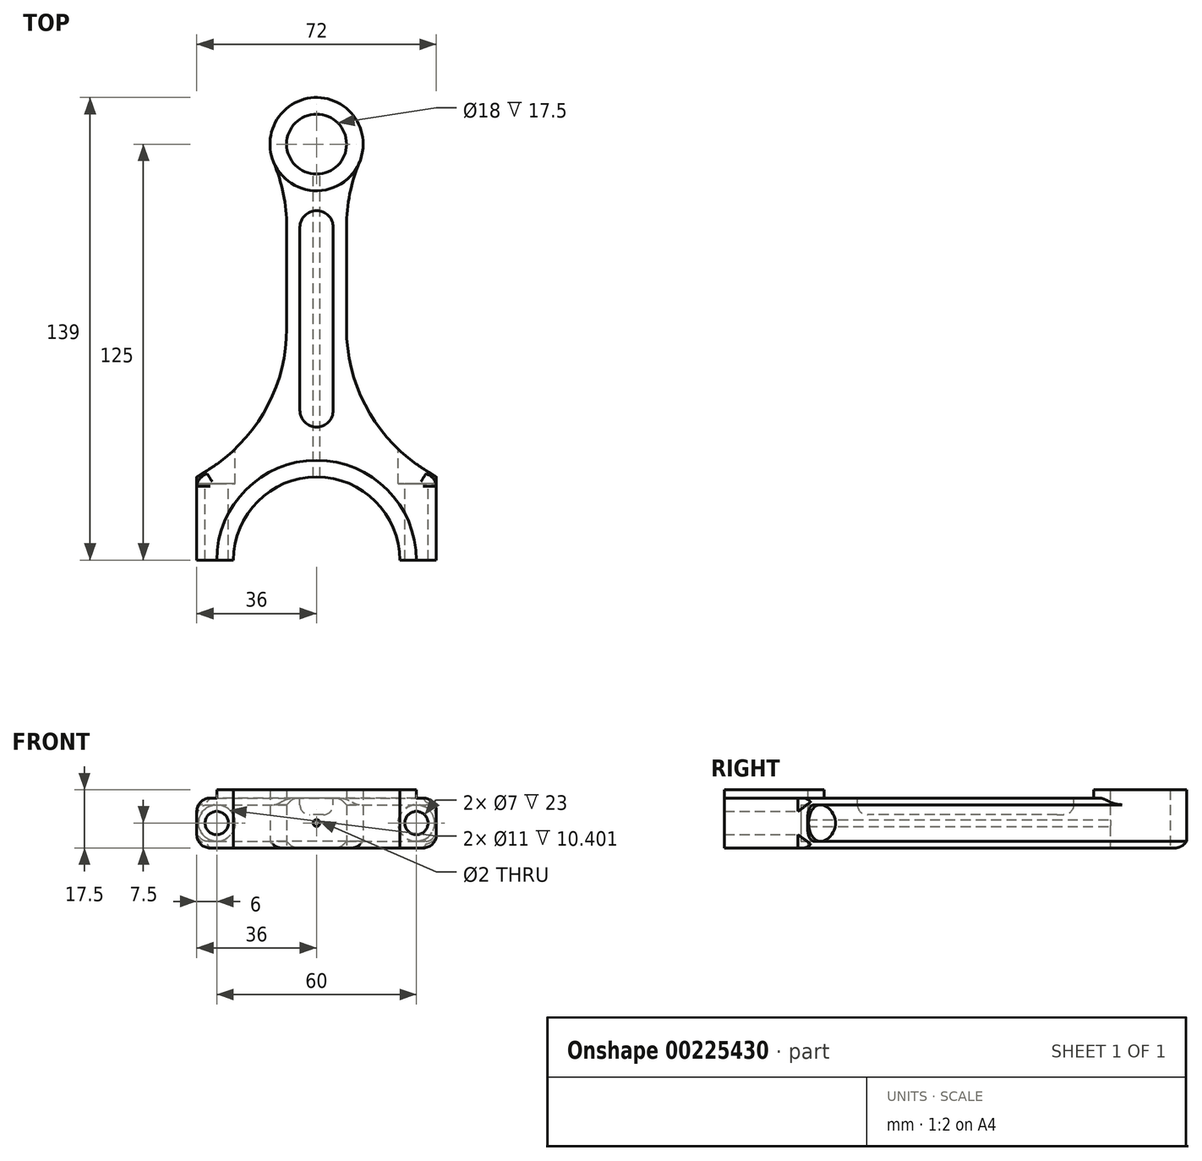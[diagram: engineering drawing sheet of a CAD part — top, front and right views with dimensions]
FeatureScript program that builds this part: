
annotation { "Feature Type Name" : "Feature", "Feature Type Description" : "" }
export const myFeature = defineFeature(function(context is Context, id is Id, definition is map)
    precondition{}
    {
        {
            var Q0;
            Q0=qCreatedBy(makeId("Top.planeOp"),FACE);
            var sketch = newSketch(context, id + "F0", { "sketchPlane" : qUnion([Q0])});
            skLineSegment(sketch, "E0", {"start": v(25, 0) * mm, "end": v(36, 0) * mm});
            skLineSegment(sketch, "E1", {"start": v(36, 0) * mm, "end": v(36, 25) * mm});
            skLineSegment(sketch, "E2", {"start": v(36, 25) * mm, "end": v(32.5, 27.19) * mm});
            skArc(sketch, "E3", {"start": v(32.5, 27.19) * mm, "mid": v(15.26, 45.35) * mm, "end": v(9, 69.59) * mm});
            skLineSegment(sketch, "E4", {"start": v(9, 69.59) * mm, "end": v(9, 100.2) * mm});
            skArc(sketch, "E5", {"start": v(9, 100.2) * mm, "mid": v(9.98, 110.08) * mm, "end": v(12.9, 119.57) * mm});
            skArc(sketch, "E6", {"start": v(12.9, 119.57) * mm, "mid": v(11.66, 132.75) * mm, "end": v(0, 139) * mm});
            skLineSegment(sketch, "E7", {"start": v(0, -25) * mm, "end": v(0, 183.63) * mm, "construction": true});
            skArc(sketch, "E8", {"start": v(25, 0) * mm, "mid": v(17.68, 17.68) * mm, "end": v(0, 25) * mm});
            skArc(sketch, "E9", {"start": v(0, 116) * mm, "mid": v(9, 125) * mm, "end": v(0, 134) * mm});
            skLineSegment(sketch, "E10.MirrorCS", {"start": v(-36, 25) * mm, "end": v(-32.5, 27.19) * mm});
            skLineSegment(sketch, "E11.MirrorCS", {"start": v(-36, 0) * mm, "end": v(-36, 25) * mm});
            skArc(sketch, "E12.MirrorCS", {"start": v(0, 116) * mm, "mid": v(-9, 125) * mm, "end": v(0, 134) * mm});
            skArc(sketch, "E13.MirrorCS", {"start": v(-25, 0) * mm, "mid": v(-17.68, 17.68) * mm, "end": v(0, 25) * mm});
            skArc(sketch, "E14.MirrorCS", {"start": v(-32.5, 27.19) * mm, "mid": v(-15.26, 45.35) * mm, "end": v(-9, 69.59) * mm});
            skLineSegment(sketch, "E15.MirrorCS", {"start": v(-25, 0) * mm, "end": v(-36, 0) * mm});
            skLineSegment(sketch, "E16.MirrorCS", {"start": v(-9, 69.59) * mm, "end": v(-9, 100.2) * mm});
            skArc(sketch, "E17.MirrorCS", {"start": v(-9, 100.2) * mm, "mid": v(-9.98, 110.08) * mm, "end": v(-12.9, 119.57) * mm});
            skArc(sketch, "E18.MirrorCS", {"start": v(-12.9, 119.57) * mm, "mid": v(-11.66, 132.75) * mm, "end": v(0, 139) * mm});
            skSolve(sketch);
        }
        {
            var Q0;
            Q0=qSketchRegion(id+"F0",true);
            extrude(context, id + "F1", {"entities" : qUnion([Q0]), "endBound" : BoundingType.SYMMETRIC, "depth" : 15 * mm});
        }
        {
            var Q0;
            Q0=makeQuery(id+"F1.opExtrude","CAP_FACE",FACE,{"disambiguationData":[OSD([sQuery(id+"F0.wireOp",EDGE,"E0"),sQuery(id+"F0.wireOp",EDGE,"E1"),sQuery(id+"F0.wireOp",EDGE,"E2"),sQuery(id+"F0.wireOp",EDGE,"E3"),sQuery(id+"F0.wireOp",EDGE,"E4"),sQuery(id+"F0.wireOp",EDGE,"E5"),sQuery(id+"F0.wireOp",EDGE,"E6"),sQuery(id+"F0.wireOp",EDGE,"E8"),sQuery(id+"F0.wireOp",EDGE,"E9"),sQuery(id+"F0.wireOp",EDGE,"E10.MirrorCS"),sQuery(id+"F0.wireOp",EDGE,"E11.MirrorCS"),sQuery(id+"F0.wireOp",EDGE,"E12.MirrorCS"),sQuery(id+"F0.wireOp",EDGE,"E13.MirrorCS"),sQuery(id+"F0.wireOp",EDGE,"E14.MirrorCS"),sQuery(id+"F0.wireOp",EDGE,"E15.MirrorCS"),sQuery(id+"F0.wireOp",EDGE,"E16.MirrorCS"),sQuery(id+"F0.wireOp",EDGE,"E17.MirrorCS"),sQuery(id+"F0.wireOp",EDGE,"E18.MirrorCS")])],"isStart":false});
            var sketch = newSketch(context, id + "F2", { "sketchPlane" : qUnion([Q0])});
            skArc(sketch, "E19", {"start": v(30, 0) * mm, "mid": v(0, 30) * mm, "end": v(-30, 0) * mm});
            skCircle(sketch, "E20", {"center": v(0, 125) * mm, "radius": 14 * mm});
            skLineSegment(sketch, "E21", {"start": v(-30, 0) * mm, "end": v(30, 0) * mm});
            skSolve(sketch);
        }
        {
            var Q0;
            Q0=makeQuery(id+"F2.imprint","IMPRINT",FACE,{"disambiguationData":[TD([[makeQuery(id+"F2.imprint","IMPRINT",EDGE,{"derivedFrom":makeQuery(id+"F1.opExtrude","CAP_EDGE",EDGE,{"disambiguationData":[OSD([sQuery(id+"F0.wireOp",EDGE,"E9"),sQuery(id+"F0.wireOp",EDGE,"E12.MirrorCS")])],"isStart":false})}),-1.0]])]});
            var Q1;
            {var subQ0=sQuery(id+"F2.wireOp",EDGE,"E19");Q1=makeQuery(id+"F2.imprint","IMPRINT",FACE,{"disambiguationData":[TD([[makeQuery(id+"F2.imprint","IMPRINT",EDGE,{"derivedFrom":subQ0}),1.0]])]});}
            extrude(context, id + "F3", {"entities" : qUnion([Q0, Q1]), "operationType" : NewBodyOperationType.ADD, "depth" : 2.5 * mm});
        }
        {
            var Q0;
            Q0=makeQuery(id+"F1.opExtrude","CAP_FACE",FACE,{"disambiguationData":[OSD([sQuery(id+"F0.wireOp",EDGE,"E0"),sQuery(id+"F0.wireOp",EDGE,"E1"),sQuery(id+"F0.wireOp",EDGE,"E2"),sQuery(id+"F0.wireOp",EDGE,"E3"),sQuery(id+"F0.wireOp",EDGE,"E4"),sQuery(id+"F0.wireOp",EDGE,"E5"),sQuery(id+"F0.wireOp",EDGE,"E6"),sQuery(id+"F0.wireOp",EDGE,"E8"),sQuery(id+"F0.wireOp",EDGE,"E9"),sQuery(id+"F0.wireOp",EDGE,"E10.MirrorCS"),sQuery(id+"F0.wireOp",EDGE,"E11.MirrorCS"),sQuery(id+"F0.wireOp",EDGE,"E12.MirrorCS"),sQuery(id+"F0.wireOp",EDGE,"E13.MirrorCS"),sQuery(id+"F0.wireOp",EDGE,"E14.MirrorCS"),sQuery(id+"F0.wireOp",EDGE,"E15.MirrorCS"),sQuery(id+"F0.wireOp",EDGE,"E16.MirrorCS"),sQuery(id+"F0.wireOp",EDGE,"E17.MirrorCS"),sQuery(id+"F0.wireOp",EDGE,"E18.MirrorCS")])],"isStart":false});
            var sketch = newSketch(context, id + "F4", { "sketchPlane" : qUnion([Q0])});
            skLineSegment(sketch, "E22.left", {"start": v(5, 100) * mm, "end": v(5, 45) * mm});
            skLineSegment(sketch, "E22.right", {"start": v(-5, 100) * mm, "end": v(-5, 45) * mm});
            skPoint(sketch, "E22.middle", {"position": v(0, 72.5) * mm});
            skArc(sketch, "E23", {"start": v(-5, 100) * mm, "mid": v(0, 105) * mm, "end": v(5, 100) * mm});
            skArc(sketch, "E24", {"start": v(-5, 45) * mm, "mid": v(0, 40) * mm, "end": v(5, 45) * mm});
            skSolve(sketch);
        }
        {
            var Q0;
            Q0=qSketchRegion(id+"F4",true);
            extrude(context, id + "F5", {"entities" : qUnion([Q0]), "operationType" : NewBodyOperationType.REMOVE, "oppositeDirection" : true, "depth" : 5 * mm});
        }
        {
            var Q0;
            Q0=makeQuery(id+"F1.opExtrude","CAP_EDGE",EDGE,{"disambiguationData":[OSD([sQuery(id+"F0.wireOp",EDGE,"E3")])],"isStart":false});
            var Q1;
            Q1=makeQuery(id+"F1.opExtrude","CAP_EDGE",EDGE,{"disambiguationData":[OSD([sQuery(id+"F0.wireOp",EDGE,"E3")])],"isStart":true});
            var Q2;
            Q2=makeQuery(id+"F1.opExtrude","CAP_EDGE",EDGE,{"disambiguationData":[OSD([sQuery(id+"F0.wireOp",EDGE,"E14.MirrorCS")])],"isStart":false});
            var Q3;
            Q3=makeQuery(id+"F1.opExtrude","CAP_EDGE",EDGE,{"disambiguationData":[OSD([sQuery(id+"F0.wireOp",EDGE,"E14.MirrorCS")])],"isStart":true});
            chamfer(context, id + "F6", {"entities" : qUnion([Q0, Q1, Q2, Q3]), "width" : 2 * mm, "tangentPropagation" : true});
        }
        {
            var Q0;
            {var subQ0=sQuery(id+"F2.wireOp",EDGE,"E21");var subQ1=sQuery(id+"F0.wireOp",EDGE,"E15.MirrorCS");var subQ2=makeQuery(id+"F2.imprint","IMPRINT",EDGE,{"disambiguationData":[TD([[makeQuery(id+"F2.imprint","INTERSECT",VERTEX,{"derivedFrom":[makeQuery(id+"F1.opExtrude","CAP_EDGE",EDGE,{"disambiguationData":[OSD([subQ1])],"isStart":false}),sQuery(id+"F2.wireOp",EDGE,"E19"),subQ0]}),1.0]])],"derivedFrom":subQ0});Q0=makeQuery(id+"FnDwNdTiISAMKlj_1.1.F3.boolean.opBoolean","MERGE",FACE,{"derivedFrom":[makeQuery(id+"F3.boolean.opBoolean","MERGE",FACE,{"derivedFrom":[makeQuery(id+"F1.opExtrude","SWEPT_FACE",FACE,{"disambiguationData":[OSD([subQ1])]}),makeQuery(id+"F3.opExtrude","SWEPT_FACE",FACE,{"disambiguationData":[OSD([subQ0]),TDD([subQ2])]})]}),makeQuery(id+"FnDwNdTiISAMKlj_1.1.F3.opExtrude","SWEPT_FACE",FACE,{"disambiguationData":[OSD([subQ0]),TDD([subQ2])]})]});}
            cPlane(context, id + "F7", {"entities" : qUnion([Q0]), "cplaneType" : CPlaneType.OFFSET, "offset" : 25 * mm, "oppositeDirection" : true, "width" : 150 * mm, "height" : 150 * mm});
        }
        {
            var Q0;
            Q0=qCreatedBy(id+"F7.planeOp",FACE);
            var sketch = newSketch(context, id + "F8", { "sketchPlane" : qUnion([Q0])});
            skPoint(sketch, "E25", {"position": v(-30, 0) * mm});
            skLineSegment(sketch, "E26", {"start": v(0, 28.75) * mm, "end": v(0, -30.74) * mm, "construction": true});
            skPoint(sketch, "E27.MirrorP", {"position": v(30, 0) * mm});
            skSolve(sketch);
        }
        {
            var Q0;
            Q0=sQuery(id+"F8.wireOp",VERTEX,"E27.MirrorP");
            var Q1;
            Q1=sQuery(id+"F8.wireOp",VERTEX,"E25");
            var Q2;
            Q2=makeQuery(id+"F1.opExtrude","SWEPT_BODY",BODY,{"disambiguationData":[OSD([sQuery(id+"F0.wireOp",EDGE,"E0"),sQuery(id+"F0.wireOp",EDGE,"E1"),sQuery(id+"F0.wireOp",EDGE,"E2"),sQuery(id+"F0.wireOp",EDGE,"E3"),sQuery(id+"F0.wireOp",EDGE,"E4"),sQuery(id+"F0.wireOp",EDGE,"E5"),sQuery(id+"F0.wireOp",EDGE,"E6"),sQuery(id+"F0.wireOp",EDGE,"E8"),sQuery(id+"F0.wireOp",EDGE,"E9"),sQuery(id+"F0.wireOp",EDGE,"E10.MirrorCS"),sQuery(id+"F0.wireOp",EDGE,"E11.MirrorCS"),sQuery(id+"F0.wireOp",EDGE,"E12.MirrorCS"),sQuery(id+"F0.wireOp",EDGE,"E13.MirrorCS"),sQuery(id+"F0.wireOp",EDGE,"E14.MirrorCS"),sQuery(id+"F0.wireOp",EDGE,"E15.MirrorCS"),sQuery(id+"F0.wireOp",EDGE,"E16.MirrorCS"),sQuery(id+"F0.wireOp",EDGE,"E17.MirrorCS"),sQuery(id+"F0.wireOp",EDGE,"E18.MirrorCS")])]});
            hole(context, id + "F9", {"style" : HoleStyle.C_BORE, "endStyle" : HoleEndStyle.THROUGH, "oppositeDirection" : true, "holeDiameter" : 7 * mm, "cBoreDiameter" : 11 * mm, "cBoreDepth" : 2 * mm, "startFromSketch" : true, "locations" : qUnion([Q0, Q1]), "scope" : qUnion([Q2]), "isTappedThrough" : true});
        }
        {
            var Q0;
            Q0=qCreatedBy(id+"F7.planeOp",FACE);
            var sketch = newSketch(context, id + "F10", { "sketchPlane" : qUnion([Q0])});
            skCircle(sketch, "E28", {"center": v(-30, 0) * mm, "radius": 5.5 * mm});
            skCircle(sketch, "E29", {"center": v(30, 0) * mm, "radius": 5.5 * mm});
            skSolve(sketch);
        }
        {
            var Q0;
            Q0=qSketchRegion(id+"F10",true);
            extrude(context, id + "F11", {"entities" : qUnion([Q0]), "operationType" : NewBodyOperationType.REMOVE, "oppositeDirection" : true, "depth" : 25 * mm});
        }
        {
            var Q0;
            Q0=makeQuery(id+"F9rkkF7bLStw4Ax_1.1.F5.boolean.opBoolean","COPY",EDGE,{"derivedFrom":makeQuery(id+"F9rkkF7bLStw4Ax_1.1.F5.opExtrude","CAP_EDGE",EDGE,{"disambiguationData":[OSD([sQuery(id+"F4.wireOp",EDGE,"E22.right")])],"isStart":false})});
            var Q1;
            Q1=makeQuery(id+"FnDwNdTiISAMKlj_1.1.F3.opExtrude","CAP_EDGE",EDGE,{"disambiguationData":[OSD([sQuery(id+"F2.wireOp",EDGE,"E19")])],"isStart":true});
            var Q2;
            Q2=makeQuery(id+"F3.opExtrude","CAP_EDGE",EDGE,{"disambiguationData":[OSD([sQuery(id+"F2.wireOp",EDGE,"E19")])],"isStart":true});
            var Q3;
            Q3=makeQuery(id+"F5.boolean.opBoolean","COPY",EDGE,{"derivedFrom":makeQuery(id+"F5.opExtrude","CAP_EDGE",EDGE,{"disambiguationData":[OSD([sQuery(id+"F4.wireOp",EDGE,"E22.right")])],"isStart":false})});
            fillet(context, id + "F12", {"entities" : qUnion([Q0, Q1, Q2, Q3]), "radius" : 3 * mm, "tangentPropagation" : true, "allowEdgeOverflow" : false});
        }
        {
            var Q0;
            Q0=makeQuery(id+"F6.opChamfer","BLEND_EDGE",EDGE,{"blendedFrom":[makeQuery(id+"F1.opExtrude","CAP_EDGE",EDGE,{"disambiguationData":[OSD([sQuery(id+"F0.wireOp",EDGE,"E2")])],"isStart":true}),makeQuery(id+"F1.opExtrude","SWEPT_FACE",FACE,{"disambiguationData":[OSD([sQuery(id+"F0.wireOp",EDGE,"E1")])]})],"blendedInto":[makeQuery(id+"F1.opExtrude","SWEPT_FACE",FACE,{"disambiguationData":[OSD([sQuery(id+"F0.wireOp",EDGE,"E1")])]})]});
            var Q1;
            Q1=makeQuery(id+"F6.opChamfer","BLEND_EDGE",EDGE,{"blendedFrom":[makeQuery(id+"F1.opExtrude","CAP_EDGE",EDGE,{"disambiguationData":[OSD([sQuery(id+"F0.wireOp",EDGE,"E2")])],"isStart":false}),makeQuery(id+"F1.opExtrude","SWEPT_FACE",FACE,{"disambiguationData":[OSD([sQuery(id+"F0.wireOp",EDGE,"E1")])]})],"blendedInto":[makeQuery(id+"F1.opExtrude","SWEPT_FACE",FACE,{"disambiguationData":[OSD([sQuery(id+"F0.wireOp",EDGE,"E1")])]})]});
            var Q2;
            Q2=makeQuery(id+"F6.opChamfer","BLEND_EDGE",EDGE,{"blendedFrom":[makeQuery(id+"F1.opExtrude","CAP_EDGE",EDGE,{"disambiguationData":[OSD([sQuery(id+"F0.wireOp",EDGE,"E10.MirrorCS")])],"isStart":true}),makeQuery(id+"F1.opExtrude","SWEPT_FACE",FACE,{"disambiguationData":[OSD([sQuery(id+"F0.wireOp",EDGE,"E11.MirrorCS")])]})],"blendedInto":[makeQuery(id+"F1.opExtrude","SWEPT_FACE",FACE,{"disambiguationData":[OSD([sQuery(id+"F0.wireOp",EDGE,"E11.MirrorCS")])]})]});
            var Q3;
            Q3=makeQuery(id+"F6.opChamfer","BLEND_EDGE",EDGE,{"blendedFrom":[makeQuery(id+"F1.opExtrude","CAP_EDGE",EDGE,{"disambiguationData":[OSD([sQuery(id+"F0.wireOp",EDGE,"E10.MirrorCS")])],"isStart":false}),makeQuery(id+"F1.opExtrude","SWEPT_FACE",FACE,{"disambiguationData":[OSD([sQuery(id+"F0.wireOp",EDGE,"E11.MirrorCS")])]})],"blendedInto":[makeQuery(id+"F1.opExtrude","SWEPT_FACE",FACE,{"disambiguationData":[OSD([sQuery(id+"F0.wireOp",EDGE,"E11.MirrorCS")])]})]});
            fillet(context, id + "F13", {"entities" : qUnion([Q0, Q1, Q2, Q3]), "radius" : 5 * mm, "tangentPropagation" : true, "allowEdgeOverflow" : false});
        }
        {
            var Q0;
            {var subQ0=sQuery(id+"F0.wireOp",EDGE,"E2");var subQ1=sQuery(id+"F0.wireOp",EDGE,"E1");Q0=makeQuery(id+"F13.opFillet","BLEND_EDGE",EDGE,{"blendedFrom":[makeQuery(id+"F6.opChamfer","BLEND_EDGE",EDGE,{"blendedFrom":[makeQuery(id+"F1.opExtrude","CAP_EDGE",EDGE,{"disambiguationData":[OSD([subQ0])],"isStart":true}),makeQuery(id+"F1.opExtrude","SWEPT_FACE",FACE,{"disambiguationData":[OSD([subQ1])]})],"blendedInto":[makeQuery(id+"F1.opExtrude","SWEPT_FACE",FACE,{"disambiguationData":[OSD([subQ1])]})]}),makeQuery(id+"F1.opExtrude","CAP_FACE",FACE,{"disambiguationData":[OSD([sQuery(id+"F0.wireOp",EDGE,"E0"),subQ1,subQ0,sQuery(id+"F0.wireOp",EDGE,"E3"),sQuery(id+"F0.wireOp",EDGE,"E4"),sQuery(id+"F0.wireOp",EDGE,"E5"),sQuery(id+"F0.wireOp",EDGE,"E6"),sQuery(id+"F0.wireOp",EDGE,"E8"),sQuery(id+"F0.wireOp",EDGE,"E9"),sQuery(id+"F0.wireOp",EDGE,"E10.MirrorCS"),sQuery(id+"F0.wireOp",EDGE,"E11.MirrorCS"),sQuery(id+"F0.wireOp",EDGE,"E12.MirrorCS"),sQuery(id+"F0.wireOp",EDGE,"E13.MirrorCS"),sQuery(id+"F0.wireOp",EDGE,"E14.MirrorCS"),sQuery(id+"F0.wireOp",EDGE,"E15.MirrorCS"),sQuery(id+"F0.wireOp",EDGE,"E16.MirrorCS"),sQuery(id+"F0.wireOp",EDGE,"E17.MirrorCS"),sQuery(id+"F0.wireOp",EDGE,"E18.MirrorCS")])],"isStart":true})],"blendedInto":[makeQuery(id+"F1.opExtrude","CAP_FACE",FACE,{"disambiguationData":[OSD([sQuery(id+"F0.wireOp",EDGE,"E0"),subQ1,subQ0,sQuery(id+"F0.wireOp",EDGE,"E3"),sQuery(id+"F0.wireOp",EDGE,"E4"),sQuery(id+"F0.wireOp",EDGE,"E5"),sQuery(id+"F0.wireOp",EDGE,"E6"),sQuery(id+"F0.wireOp",EDGE,"E8"),sQuery(id+"F0.wireOp",EDGE,"E9"),sQuery(id+"F0.wireOp",EDGE,"E10.MirrorCS"),sQuery(id+"F0.wireOp",EDGE,"E11.MirrorCS"),sQuery(id+"F0.wireOp",EDGE,"E12.MirrorCS"),sQuery(id+"F0.wireOp",EDGE,"E13.MirrorCS"),sQuery(id+"F0.wireOp",EDGE,"E14.MirrorCS"),sQuery(id+"F0.wireOp",EDGE,"E15.MirrorCS"),sQuery(id+"F0.wireOp",EDGE,"E16.MirrorCS"),sQuery(id+"F0.wireOp",EDGE,"E17.MirrorCS"),sQuery(id+"F0.wireOp",EDGE,"E18.MirrorCS")])],"isStart":true})]});}
            var Q1;
            {var subQ0=sQuery(id+"F0.wireOp",EDGE,"E11.MirrorCS");var subQ1=sQuery(id+"F0.wireOp",EDGE,"E10.MirrorCS");Q1=makeQuery(id+"F13.opFillet","BLEND_EDGE",EDGE,{"blendedFrom":[makeQuery(id+"F6.opChamfer","BLEND_EDGE",EDGE,{"blendedFrom":[makeQuery(id+"F1.opExtrude","CAP_EDGE",EDGE,{"disambiguationData":[OSD([subQ1])],"isStart":true}),makeQuery(id+"F1.opExtrude","SWEPT_FACE",FACE,{"disambiguationData":[OSD([subQ0])]})],"blendedInto":[makeQuery(id+"F1.opExtrude","SWEPT_FACE",FACE,{"disambiguationData":[OSD([subQ0])]})]}),makeQuery(id+"F1.opExtrude","CAP_FACE",FACE,{"disambiguationData":[OSD([sQuery(id+"F0.wireOp",EDGE,"E0"),sQuery(id+"F0.wireOp",EDGE,"E1"),sQuery(id+"F0.wireOp",EDGE,"E2"),sQuery(id+"F0.wireOp",EDGE,"E3"),sQuery(id+"F0.wireOp",EDGE,"E4"),sQuery(id+"F0.wireOp",EDGE,"E5"),sQuery(id+"F0.wireOp",EDGE,"E6"),sQuery(id+"F0.wireOp",EDGE,"E8"),sQuery(id+"F0.wireOp",EDGE,"E9"),subQ1,subQ0,sQuery(id+"F0.wireOp",EDGE,"E12.MirrorCS"),sQuery(id+"F0.wireOp",EDGE,"E13.MirrorCS"),sQuery(id+"F0.wireOp",EDGE,"E14.MirrorCS"),sQuery(id+"F0.wireOp",EDGE,"E15.MirrorCS"),sQuery(id+"F0.wireOp",EDGE,"E16.MirrorCS"),sQuery(id+"F0.wireOp",EDGE,"E17.MirrorCS"),sQuery(id+"F0.wireOp",EDGE,"E18.MirrorCS")])],"isStart":true})],"blendedInto":[makeQuery(id+"F1.opExtrude","CAP_FACE",FACE,{"disambiguationData":[OSD([sQuery(id+"F0.wireOp",EDGE,"E0"),sQuery(id+"F0.wireOp",EDGE,"E1"),sQuery(id+"F0.wireOp",EDGE,"E2"),sQuery(id+"F0.wireOp",EDGE,"E3"),sQuery(id+"F0.wireOp",EDGE,"E4"),sQuery(id+"F0.wireOp",EDGE,"E5"),sQuery(id+"F0.wireOp",EDGE,"E6"),sQuery(id+"F0.wireOp",EDGE,"E8"),sQuery(id+"F0.wireOp",EDGE,"E9"),subQ1,subQ0,sQuery(id+"F0.wireOp",EDGE,"E12.MirrorCS"),sQuery(id+"F0.wireOp",EDGE,"E13.MirrorCS"),sQuery(id+"F0.wireOp",EDGE,"E14.MirrorCS"),sQuery(id+"F0.wireOp",EDGE,"E15.MirrorCS"),sQuery(id+"F0.wireOp",EDGE,"E16.MirrorCS"),sQuery(id+"F0.wireOp",EDGE,"E17.MirrorCS"),sQuery(id+"F0.wireOp",EDGE,"E18.MirrorCS")])],"isStart":true})]});}
            var Q2;
            {var subQ0=sQuery(id+"F0.wireOp",EDGE,"E11.MirrorCS");var subQ1=sQuery(id+"F0.wireOp",EDGE,"E10.MirrorCS");Q2=makeQuery(id+"F13.opFillet","BLEND_EDGE",EDGE,{"blendedFrom":[makeQuery(id+"F6.opChamfer","BLEND_EDGE",EDGE,{"blendedFrom":[makeQuery(id+"F1.opExtrude","CAP_EDGE",EDGE,{"disambiguationData":[OSD([subQ1])],"isStart":false}),makeQuery(id+"F1.opExtrude","SWEPT_FACE",FACE,{"disambiguationData":[OSD([subQ0])]})],"blendedInto":[makeQuery(id+"F1.opExtrude","SWEPT_FACE",FACE,{"disambiguationData":[OSD([subQ0])]})]}),makeQuery(id+"F1.opExtrude","CAP_FACE",FACE,{"disambiguationData":[OSD([sQuery(id+"F0.wireOp",EDGE,"E0"),sQuery(id+"F0.wireOp",EDGE,"E1"),sQuery(id+"F0.wireOp",EDGE,"E2"),sQuery(id+"F0.wireOp",EDGE,"E3"),sQuery(id+"F0.wireOp",EDGE,"E4"),sQuery(id+"F0.wireOp",EDGE,"E5"),sQuery(id+"F0.wireOp",EDGE,"E6"),sQuery(id+"F0.wireOp",EDGE,"E8"),sQuery(id+"F0.wireOp",EDGE,"E9"),subQ1,subQ0,sQuery(id+"F0.wireOp",EDGE,"E12.MirrorCS"),sQuery(id+"F0.wireOp",EDGE,"E13.MirrorCS"),sQuery(id+"F0.wireOp",EDGE,"E14.MirrorCS"),sQuery(id+"F0.wireOp",EDGE,"E15.MirrorCS"),sQuery(id+"F0.wireOp",EDGE,"E16.MirrorCS"),sQuery(id+"F0.wireOp",EDGE,"E17.MirrorCS"),sQuery(id+"F0.wireOp",EDGE,"E18.MirrorCS")])],"isStart":false})],"blendedInto":[makeQuery(id+"F1.opExtrude","CAP_FACE",FACE,{"disambiguationData":[OSD([sQuery(id+"F0.wireOp",EDGE,"E0"),sQuery(id+"F0.wireOp",EDGE,"E1"),sQuery(id+"F0.wireOp",EDGE,"E2"),sQuery(id+"F0.wireOp",EDGE,"E3"),sQuery(id+"F0.wireOp",EDGE,"E4"),sQuery(id+"F0.wireOp",EDGE,"E5"),sQuery(id+"F0.wireOp",EDGE,"E6"),sQuery(id+"F0.wireOp",EDGE,"E8"),sQuery(id+"F0.wireOp",EDGE,"E9"),subQ1,subQ0,sQuery(id+"F0.wireOp",EDGE,"E12.MirrorCS"),sQuery(id+"F0.wireOp",EDGE,"E13.MirrorCS"),sQuery(id+"F0.wireOp",EDGE,"E14.MirrorCS"),sQuery(id+"F0.wireOp",EDGE,"E15.MirrorCS"),sQuery(id+"F0.wireOp",EDGE,"E16.MirrorCS"),sQuery(id+"F0.wireOp",EDGE,"E17.MirrorCS"),sQuery(id+"F0.wireOp",EDGE,"E18.MirrorCS")])],"isStart":false})]});}
            var Q3;
            {var subQ0=sQuery(id+"F0.wireOp",EDGE,"E2");var subQ1=sQuery(id+"F0.wireOp",EDGE,"E1");Q3=makeQuery(id+"F13.opFillet","BLEND_EDGE",EDGE,{"blendedFrom":[makeQuery(id+"F6.opChamfer","BLEND_EDGE",EDGE,{"blendedFrom":[makeQuery(id+"F1.opExtrude","CAP_EDGE",EDGE,{"disambiguationData":[OSD([subQ0])],"isStart":false}),makeQuery(id+"F1.opExtrude","SWEPT_FACE",FACE,{"disambiguationData":[OSD([subQ1])]})],"blendedInto":[makeQuery(id+"F1.opExtrude","SWEPT_FACE",FACE,{"disambiguationData":[OSD([subQ1])]})]}),makeQuery(id+"F1.opExtrude","CAP_FACE",FACE,{"disambiguationData":[OSD([sQuery(id+"F0.wireOp",EDGE,"E0"),subQ1,subQ0,sQuery(id+"F0.wireOp",EDGE,"E3"),sQuery(id+"F0.wireOp",EDGE,"E4"),sQuery(id+"F0.wireOp",EDGE,"E5"),sQuery(id+"F0.wireOp",EDGE,"E6"),sQuery(id+"F0.wireOp",EDGE,"E8"),sQuery(id+"F0.wireOp",EDGE,"E9"),sQuery(id+"F0.wireOp",EDGE,"E10.MirrorCS"),sQuery(id+"F0.wireOp",EDGE,"E11.MirrorCS"),sQuery(id+"F0.wireOp",EDGE,"E12.MirrorCS"),sQuery(id+"F0.wireOp",EDGE,"E13.MirrorCS"),sQuery(id+"F0.wireOp",EDGE,"E14.MirrorCS"),sQuery(id+"F0.wireOp",EDGE,"E15.MirrorCS"),sQuery(id+"F0.wireOp",EDGE,"E16.MirrorCS"),sQuery(id+"F0.wireOp",EDGE,"E17.MirrorCS"),sQuery(id+"F0.wireOp",EDGE,"E18.MirrorCS")])],"isStart":false})],"blendedInto":[makeQuery(id+"F1.opExtrude","CAP_FACE",FACE,{"disambiguationData":[OSD([sQuery(id+"F0.wireOp",EDGE,"E0"),subQ1,subQ0,sQuery(id+"F0.wireOp",EDGE,"E3"),sQuery(id+"F0.wireOp",EDGE,"E4"),sQuery(id+"F0.wireOp",EDGE,"E5"),sQuery(id+"F0.wireOp",EDGE,"E6"),sQuery(id+"F0.wireOp",EDGE,"E8"),sQuery(id+"F0.wireOp",EDGE,"E9"),sQuery(id+"F0.wireOp",EDGE,"E10.MirrorCS"),sQuery(id+"F0.wireOp",EDGE,"E11.MirrorCS"),sQuery(id+"F0.wireOp",EDGE,"E12.MirrorCS"),sQuery(id+"F0.wireOp",EDGE,"E13.MirrorCS"),sQuery(id+"F0.wireOp",EDGE,"E14.MirrorCS"),sQuery(id+"F0.wireOp",EDGE,"E15.MirrorCS"),sQuery(id+"F0.wireOp",EDGE,"E16.MirrorCS"),sQuery(id+"F0.wireOp",EDGE,"E17.MirrorCS"),sQuery(id+"F0.wireOp",EDGE,"E18.MirrorCS")])],"isStart":false})]});}
            fillet(context, id + "F14", {"entities" : qUnion([Q0, Q1, Q2, Q3]), "radius" : 4 * mm, "tangentPropagation" : true, "allowEdgeOverflow" : false});
        }
        {
            var Q0;
            {var subQ0=sQuery(id+"F2.wireOp",EDGE,"E19");Q0=makeQuery(id+"F12.opFillet","BLEND_EDGE",EDGE,{"blendedFrom":[makeQuery(id+"F3.opExtrude","CAP_EDGE",EDGE,{"disambiguationData":[OSD([subQ0])],"isStart":true}),makeQuery(id+"F3.opExtrude","CAP_FACE",FACE,{"disambiguationData":[OSD([sQuery(id+"F0.wireOp",EDGE,"E8"),sQuery(id+"F0.wireOp",EDGE,"E13.MirrorCS"),subQ0,sQuery(id+"F2.wireOp",EDGE,"E21")])],"isStart":false})],"blendedInto":[makeQuery(id+"F3.opExtrude","CAP_FACE",FACE,{"disambiguationData":[OSD([sQuery(id+"F0.wireOp",EDGE,"E8"),sQuery(id+"F0.wireOp",EDGE,"E13.MirrorCS"),subQ0,sQuery(id+"F2.wireOp",EDGE,"E21")])],"isStart":false})]});}
            var Q1;
            Q1=makeQuery(id+"F3.opExtrude","CAP_EDGE",EDGE,{"disambiguationData":[OSD([sQuery(id+"F0.wireOp",EDGE,"E8"),sQuery(id+"F0.wireOp",EDGE,"E13.MirrorCS")])],"isStart":false});
            var Q2;
            Q2=makeQuery(id+"FnDwNdTiISAMKlj_1.1.F3.opExtrude","CAP_EDGE",EDGE,{"disambiguationData":[OSD([sQuery(id+"F0.wireOp",EDGE,"E8"),sQuery(id+"F0.wireOp",EDGE,"E13.MirrorCS")])],"isStart":false});
            var Q3;
            {var subQ0=sQuery(id+"F2.wireOp",EDGE,"E19");Q3=makeQuery(id+"F12.opFillet","BLEND_EDGE",EDGE,{"blendedFrom":[makeQuery(id+"FnDwNdTiISAMKlj_1.1.F3.opExtrude","CAP_EDGE",EDGE,{"disambiguationData":[OSD([subQ0])],"isStart":true}),makeQuery(id+"FnDwNdTiISAMKlj_1.1.F3.opExtrude","CAP_FACE",FACE,{"disambiguationData":[OSD([sQuery(id+"F0.wireOp",EDGE,"E8"),sQuery(id+"F0.wireOp",EDGE,"E13.MirrorCS"),subQ0,sQuery(id+"F2.wireOp",EDGE,"E21")])],"isStart":false})],"blendedInto":[makeQuery(id+"FnDwNdTiISAMKlj_1.1.F3.opExtrude","CAP_FACE",FACE,{"disambiguationData":[OSD([sQuery(id+"F0.wireOp",EDGE,"E8"),sQuery(id+"F0.wireOp",EDGE,"E13.MirrorCS"),subQ0,sQuery(id+"F2.wireOp",EDGE,"E21")])],"isStart":false})]});}
            fillet(context, id + "F15", {"entities" : qUnion([Q0, Q1, Q2, Q3]), "radius" : .3 * mm, "tangentPropagation" : true, "allowEdgeOverflow" : false});
        }
        {
            var Q0;
            {var subQ0=sQuery(id+"F2.wireOp",EDGE,"E21");var subQ1=sQuery(id+"F0.wireOp",EDGE,"E15.MirrorCS");var subQ2=makeQuery(id+"F2.imprint","IMPRINT",EDGE,{"disambiguationData":[TD([[makeQuery(id+"F2.imprint","INTERSECT",VERTEX,{"derivedFrom":[makeQuery(id+"F1.opExtrude","CAP_EDGE",EDGE,{"disambiguationData":[OSD([subQ1])],"isStart":false}),sQuery(id+"F2.wireOp",EDGE,"E19"),subQ0]}),1.0]])],"derivedFrom":subQ0});Q0=makeQuery(id+"FnDwNdTiISAMKlj_1.1.F3.boolean.opBoolean","MERGE",FACE,{"derivedFrom":[makeQuery(id+"F3.boolean.opBoolean","MERGE",FACE,{"derivedFrom":[makeQuery(id+"F1.opExtrude","SWEPT_FACE",FACE,{"disambiguationData":[OSD([subQ1])]}),makeQuery(id+"F3.opExtrude","SWEPT_FACE",FACE,{"disambiguationData":[OSD([subQ0]),TDD([subQ2])]})]}),makeQuery(id+"FnDwNdTiISAMKlj_1.1.F3.opExtrude","SWEPT_FACE",FACE,{"disambiguationData":[OSD([subQ0]),TDD([subQ2])]})]});}
            cPlane(context, id + "F16", {"entities" : qUnion([Q0]), "cplaneType" : CPlaneType.OFFSET, "offset" : 125 * mm, "oppositeDirection" : true, "width" : 150 * mm, "height" : 150 * mm});
        }
        {
            var Q0;
            Q0=qCreatedBy(id+"F16.planeOp",FACE);
            var sketch = newSketch(context, id + "F17", { "sketchPlane" : qUnion([Q0])});
            skCircle(sketch, "E30", {"center": v(0, 0) * mm, "radius": 1 * mm});
            skSolve(sketch);
        }
        {
            var Q0;
            Q0=qSketchRegion(id+"F17",true);
            extrude(context, id + "F18", {"entities" : qUnion([Q0]), "operationType" : NewBodyOperationType.REMOVE, "endBound" : BoundingType.THROUGH_ALL, "depth" : 25 * mm});
        }
    });
